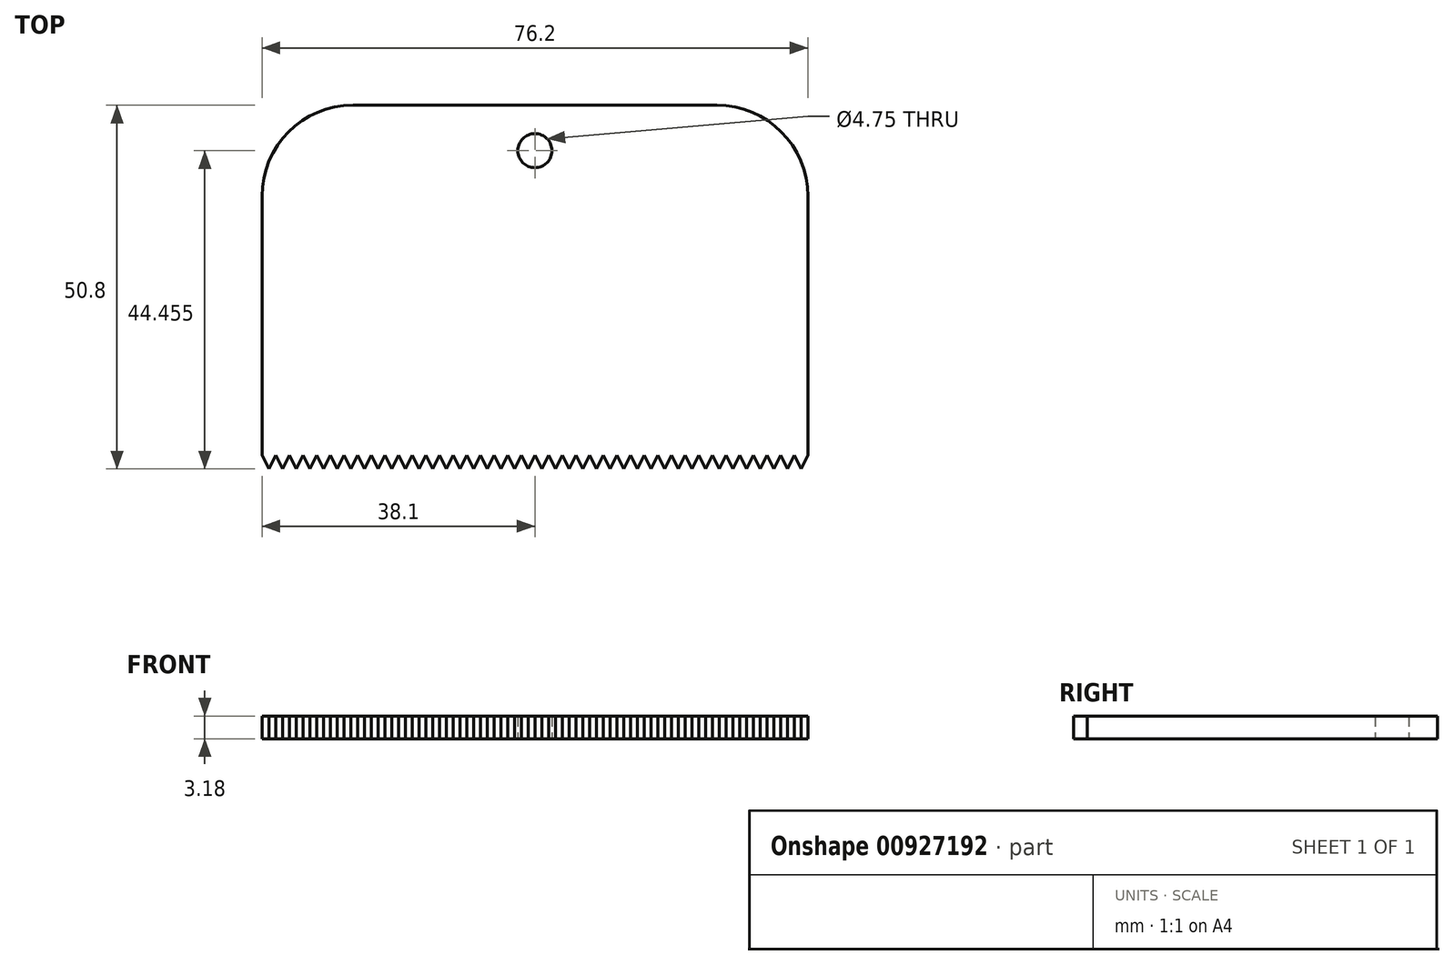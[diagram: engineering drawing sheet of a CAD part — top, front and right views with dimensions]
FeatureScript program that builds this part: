
annotation { "Feature Type Name" : "Feature", "Feature Type Description" : "" }
export const myFeature = defineFeature(function(context is Context, id is Id, definition is map)
    precondition{}
    {
        {
            var Q0;
            Q0=qCreatedBy(makeId("Top.planeOp"),FACE);
            var sketch = newSketch(context, id + "F0", { "sketchPlane" : qUnion([Q0])});
            skLineSegment(sketch, "E0.bottom", {"start": v(38.1, -9.52) * mm, "end": v(-38.1, -9.53) * mm});
            skLineSegment(sketch, "E0.left", {"start": v(38.1, -9.52) * mm, "end": v(38.1, 28.58) * mm});
            skLineSegment(sketch, "E0.right", {"start": v(-38.1, -9.53) * mm, "end": v(-38.1, 28.58) * mm});
            skPoint(sketch, "E0.middle", {"position": v(0, 0) * mm});
            skLineSegment(sketch, "E1", {"start": v(-25.4, 41.28) * mm, "end": v(3.32, 41.28) * mm});
            skPoint(sketch, "E2.orphan", {"position": v(-38.1, 9.52) * mm});
            skPoint(sketch, "E3.orphan", {"position": v(38.1, 9.53) * mm});
            skLineSegment(sketch, "E4.trimOffspring", {"start": v(3.32, 41.28) * mm, "end": v(25.4, 41.28) * mm});
            skPoint(sketch, "E5.visualSharp", {"position": v(-38.1, 41.28) * mm});
            skArc(sketch, "E5.filletArc", {"start": v(-25.4, 41.28) * mm, "mid": v(-34.38, 37.56) * mm, "end": v(-38.1, 28.58) * mm});
            skPoint(sketch, "E6.visualSharp", {"position": v(38.1, 41.28) * mm});
            skArc(sketch, "E6.filletArc", {"start": v(38.1, 28.58) * mm, "mid": v(34.38, 37.56) * mm, "end": v(25.4, 41.28) * mm});
            skCircle(sketch, "E7", {"center": v(0, 34.93) * mm, "radius": 2.37 * mm});
            skSolve(sketch);
        }
        {
            var Q0;
            Q0=makeQuery(id+"F0.imprint","IMPRINT",FACE,{"disambiguationData":[TD([[makeQuery(id+"F0.imprint","IMPRINT",EDGE,{"derivedFrom":sQuery(id+"F0.wireOp",EDGE,"E0.bottom")}),-1.0]])]});
            extrude(context, id + "F1", {"entities" : qUnion([Q0]), "depth" : 3.17 * mm, "offsetDistance" : 25.4 * mm});
        }
        {
            var Q0;
            Q0=makeQuery(id+"F1.opExtrude","CAP_FACE",FACE,{"disambiguationData":[OSD([sQuery(id+"F0.wireOp",EDGE,"E0.bottom"),sQuery(id+"F0.wireOp",EDGE,"E0.left"),sQuery(id+"F0.wireOp",EDGE,"E0.right"),sQuery(id+"F0.wireOp",EDGE,"E1"),sQuery(id+"F0.wireOp",EDGE,"E4.trimOffspring"),sQuery(id+"F0.wireOp",EDGE,"E5.filletArc"),sQuery(id+"F0.wireOp",EDGE,"E6.filletArc"),sQuery(id+"F0.wireOp",EDGE,"E7"),sQuery(id+"F0.wireOp",EDGE,"qO9MC2i9-FNPQ-Q0Oo-eFE0-4rk33zHTfKXJ"),sQuery(id+"F0.wireOp",EDGE,"a6c80942-7ec7-4028-b4f8-ebce8057ab8d.filletArc"),sQuery(id+"F0.wireOp",EDGE,"d8f89c69-07ce-40ea-bba9-d7924d7e0f25.filletArc")])],"isStart":false});
            var sketch = newSketch(context, id + "F2", { "sketchPlane" : qUnion([Q0])});
            skLineSegment(sketch, "E8.top", {"start": v(-38.1, -14.15) * mm, "end": v(38.1, -14.15) * mm});
            skLineSegment(sketch, "E8.left", {"start": v(-38.1, -7.62) * mm, "end": v(-38.1, -14.15) * mm});
            skLineSegment(sketch, "E8.right", {"start": v(38.1, -7.62) * mm, "end": v(38.1, -14.15) * mm});
            skLineSegment(sketch, "E9", {"start": v(-38.1, -7.62) * mm, "end": v(-37.15, -9.52) * mm});
            skLineSegment(sketch, "E10", {"start": v(-38.1, -7.62) * mm, "end": v(-39.05, -9.53) * mm});
            skLineSegment(sketch, "E11.1.0.0", {"start": v(-36.2, -7.62) * mm, "end": v(-35.24, -9.52) * mm});
            skLineSegment(sketch, "E11.1.0.1", {"start": v(-36.2, -7.62) * mm, "end": v(-37.15, -9.53) * mm});
            skLineSegment(sketch, "E11.2.0.0", {"start": v(-34.29, -7.62) * mm, "end": v(-33.34, -9.52) * mm});
            skLineSegment(sketch, "E11.2.0.1", {"start": v(-34.29, -7.62) * mm, "end": v(-35.24, -9.53) * mm});
            skLineSegment(sketch, "E11.3.0.0", {"start": v(-32.38, -7.62) * mm, "end": v(-31.43, -9.52) * mm});
            skLineSegment(sketch, "E11.3.0.1", {"start": v(-32.38, -7.62) * mm, "end": v(-33.34, -9.53) * mm});
            skLineSegment(sketch, "E11.4.0.0", {"start": v(-30.48, -7.62) * mm, "end": v(-29.53, -9.53) * mm});
            skLineSegment(sketch, "E11.4.0.1", {"start": v(-30.48, -7.62) * mm, "end": v(-31.43, -9.53) * mm});
            skLineSegment(sketch, "E11.5.0.0", {"start": v(-28.57, -7.62) * mm, "end": v(-27.62, -9.53) * mm});
            skLineSegment(sketch, "E11.5.0.1", {"start": v(-28.57, -7.62) * mm, "end": v(-29.53, -9.53) * mm});
            skLineSegment(sketch, "E11.6.0.0", {"start": v(-26.67, -7.62) * mm, "end": v(-25.72, -9.53) * mm});
            skLineSegment(sketch, "E11.6.0.1", {"start": v(-26.67, -7.62) * mm, "end": v(-27.62, -9.53) * mm});
            skLineSegment(sketch, "E11.7.0.0", {"start": v(-24.76, -7.62) * mm, "end": v(-23.81, -9.53) * mm});
            skLineSegment(sketch, "E11.7.0.1", {"start": v(-24.76, -7.62) * mm, "end": v(-25.72, -9.53) * mm});
            skLineSegment(sketch, "E11.8.0.0", {"start": v(-22.86, -7.62) * mm, "end": v(-21.9, -9.53) * mm});
            skLineSegment(sketch, "E11.8.0.1", {"start": v(-22.86, -7.62) * mm, "end": v(-23.81, -9.53) * mm});
            skLineSegment(sketch, "E11.9.0.0", {"start": v(-20.95, -7.62) * mm, "end": v(-20, -9.53) * mm});
            skLineSegment(sketch, "E11.9.0.1", {"start": v(-20.95, -7.62) * mm, "end": v(-21.9, -9.53) * mm});
            skLineSegment(sketch, "E11.10.0.0", {"start": v(-19.05, -7.62) * mm, "end": v(-18.1, -9.53) * mm});
            skLineSegment(sketch, "E11.10.0.1", {"start": v(-19.05, -7.62) * mm, "end": v(-20, -9.53) * mm});
            skLineSegment(sketch, "E11.11.0.0", {"start": v(-17.14, -7.62) * mm, "end": v(-16.2, -9.53) * mm});
            skLineSegment(sketch, "E11.11.0.1", {"start": v(-17.14, -7.62) * mm, "end": v(-18.1, -9.53) * mm});
            skLineSegment(sketch, "E11.12.0.0", {"start": v(-15.24, -7.62) * mm, "end": v(-14.29, -9.53) * mm});
            skLineSegment(sketch, "E11.12.0.1", {"start": v(-15.24, -7.62) * mm, "end": v(-16.2, -9.53) * mm});
            skLineSegment(sketch, "E11.13.0.0", {"start": v(-13.33, -7.62) * mm, "end": v(-12.38, -9.53) * mm});
            skLineSegment(sketch, "E11.13.0.1", {"start": v(-13.33, -7.62) * mm, "end": v(-14.29, -9.53) * mm});
            skLineSegment(sketch, "E11.14.0.0", {"start": v(-11.43, -7.62) * mm, "end": v(-10.48, -9.53) * mm});
            skLineSegment(sketch, "E11.14.0.1", {"start": v(-11.43, -7.62) * mm, "end": v(-12.38, -9.53) * mm});
            skLineSegment(sketch, "E11.15.0.0", {"start": v(-9.52, -7.62) * mm, "end": v(-8.57, -9.53) * mm});
            skLineSegment(sketch, "E11.15.0.1", {"start": v(-9.52, -7.62) * mm, "end": v(-10.48, -9.53) * mm});
            skLineSegment(sketch, "E11.16.0.0", {"start": v(-7.62, -7.62) * mm, "end": v(-6.67, -9.53) * mm});
            skLineSegment(sketch, "E11.16.0.1", {"start": v(-7.62, -7.62) * mm, "end": v(-8.57, -9.53) * mm});
            skLineSegment(sketch, "E11.17.0.0", {"start": v(-5.71, -7.62) * mm, "end": v(-4.76, -9.53) * mm});
            skLineSegment(sketch, "E11.17.0.1", {"start": v(-5.71, -7.62) * mm, "end": v(-6.67, -9.53) * mm});
            skLineSegment(sketch, "E11.18.0.0", {"start": v(-3.8, -7.62) * mm, "end": v(-2.86, -9.53) * mm});
            skLineSegment(sketch, "E11.18.0.1", {"start": v(-3.8, -7.62) * mm, "end": v(-4.76, -9.53) * mm});
            skLineSegment(sketch, "E11.19.0.0", {"start": v(-1.9, -7.62) * mm, "end": v(-0.95, -9.53) * mm});
            skLineSegment(sketch, "E11.19.0.1", {"start": v(-1.9, -7.62) * mm, "end": v(-2.86, -9.53) * mm});
            skLineSegment(sketch, "E11.20.0.0", {"start": v(0, -7.62) * mm, "end": v(0.95, -9.53) * mm});
            skLineSegment(sketch, "E11.20.0.1", {"start": v(0, -7.62) * mm, "end": v(-0.95, -9.53) * mm});
            skLineSegment(sketch, "E11.21.0.0", {"start": v(1.9, -7.62) * mm, "end": v(2.86, -9.53) * mm});
            skLineSegment(sketch, "E11.21.0.1", {"start": v(1.9, -7.62) * mm, "end": v(0.95, -9.53) * mm});
            skLineSegment(sketch, "E11.22.0.0", {"start": v(3.81, -7.62) * mm, "end": v(4.76, -9.53) * mm});
            skLineSegment(sketch, "E11.22.0.1", {"start": v(3.81, -7.62) * mm, "end": v(2.86, -9.53) * mm});
            skLineSegment(sketch, "E11.23.0.0", {"start": v(5.72, -7.62) * mm, "end": v(6.67, -9.53) * mm});
            skLineSegment(sketch, "E11.23.0.1", {"start": v(5.72, -7.62) * mm, "end": v(4.76, -9.53) * mm});
            skLineSegment(sketch, "E11.24.0.0", {"start": v(7.62, -7.62) * mm, "end": v(8.57, -9.52) * mm});
            skLineSegment(sketch, "E11.24.0.1", {"start": v(7.62, -7.62) * mm, "end": v(6.67, -9.53) * mm});
            skLineSegment(sketch, "E11.25.0.0", {"start": v(9.53, -7.62) * mm, "end": v(10.48, -9.53) * mm});
            skLineSegment(sketch, "E11.25.0.1", {"start": v(9.53, -7.62) * mm, "end": v(8.57, -9.53) * mm});
            skLineSegment(sketch, "E11.26.0.0", {"start": v(11.43, -7.62) * mm, "end": v(12.38, -9.52) * mm});
            skLineSegment(sketch, "E11.26.0.1", {"start": v(11.43, -7.62) * mm, "end": v(10.48, -9.53) * mm});
            skLineSegment(sketch, "E11.27.0.0", {"start": v(13.34, -7.62) * mm, "end": v(14.29, -9.53) * mm});
            skLineSegment(sketch, "E11.27.0.1", {"start": v(13.33, -7.62) * mm, "end": v(12.38, -9.53) * mm});
            skLineSegment(sketch, "E11.28.0.0", {"start": v(15.24, -7.62) * mm, "end": v(16.2, -9.52) * mm});
            skLineSegment(sketch, "E11.28.0.1", {"start": v(15.24, -7.62) * mm, "end": v(14.29, -9.53) * mm});
            skLineSegment(sketch, "E11.29.0.0", {"start": v(17.15, -7.62) * mm, "end": v(18.1, -9.53) * mm});
            skLineSegment(sketch, "E11.29.0.1", {"start": v(17.14, -7.62) * mm, "end": v(16.2, -9.53) * mm});
            skLineSegment(sketch, "E11.30.0.0", {"start": v(19.05, -7.62) * mm, "end": v(20, -9.52) * mm});
            skLineSegment(sketch, "E11.30.0.1", {"start": v(19.05, -7.62) * mm, "end": v(18.1, -9.53) * mm});
            skLineSegment(sketch, "E11.31.0.0", {"start": v(20.96, -7.62) * mm, "end": v(21.9, -9.53) * mm});
            skLineSegment(sketch, "E11.31.0.1", {"start": v(20.95, -7.62) * mm, "end": v(20, -9.53) * mm});
            skLineSegment(sketch, "E11.32.0.0", {"start": v(22.86, -7.62) * mm, "end": v(23.81, -9.52) * mm});
            skLineSegment(sketch, "E11.32.0.1", {"start": v(22.86, -7.62) * mm, "end": v(21.9, -9.53) * mm});
            skLineSegment(sketch, "E11.33.0.0", {"start": v(24.77, -7.62) * mm, "end": v(25.72, -9.53) * mm});
            skLineSegment(sketch, "E11.33.0.1", {"start": v(24.76, -7.62) * mm, "end": v(23.81, -9.53) * mm});
            skLineSegment(sketch, "E11.34.0.0", {"start": v(26.67, -7.62) * mm, "end": v(27.62, -9.53) * mm});
            skLineSegment(sketch, "E11.34.0.1", {"start": v(26.67, -7.62) * mm, "end": v(25.72, -9.53) * mm});
            skLineSegment(sketch, "E11.35.0.0", {"start": v(28.58, -7.62) * mm, "end": v(29.53, -9.53) * mm});
            skLineSegment(sketch, "E11.35.0.1", {"start": v(28.57, -7.62) * mm, "end": v(27.62, -9.53) * mm});
            skLineSegment(sketch, "E11.36.0.0", {"start": v(30.48, -7.62) * mm, "end": v(31.43, -9.53) * mm});
            skLineSegment(sketch, "E11.36.0.1", {"start": v(30.48, -7.62) * mm, "end": v(29.53, -9.53) * mm});
            skLineSegment(sketch, "E11.37.0.0", {"start": v(32.38, -7.62) * mm, "end": v(33.34, -9.53) * mm});
            skLineSegment(sketch, "E11.37.0.1", {"start": v(32.38, -7.62) * mm, "end": v(31.43, -9.53) * mm});
            skLineSegment(sketch, "E11.38.0.0", {"start": v(34.3, -7.62) * mm, "end": v(35.24, -9.52) * mm});
            skLineSegment(sketch, "E11.38.0.1", {"start": v(34.29, -7.62) * mm, "end": v(33.34, -9.53) * mm});
            skLineSegment(sketch, "E11.39.0.0", {"start": v(36.2, -7.62) * mm, "end": v(37.15, -9.53) * mm});
            skLineSegment(sketch, "E11.39.0.1", {"start": v(36.2, -7.62) * mm, "end": v(35.24, -9.53) * mm});
            skLineSegment(sketch, "E11.40.0.1", {"start": v(38.1, -7.62) * mm, "end": v(37.15, -9.53) * mm});
            skLineSegment(sketch, "E11.direction1", {"start": v(-39.05, -9.53) * mm, "end": v(-37.15, -9.53) * mm, "construction": true});
            skSolve(sketch);
        }
        {
            var Q0;
            Q0=qSketchRegion(id+"F2",true);
            extrude(context, id + "F3", {"entities" : qUnion([Q0]), "operationType" : NewBodyOperationType.REMOVE, "oppositeDirection" : true, "depth" : 25.4 * mm, "offsetDistance" : 25.4 * mm});
        }
    });
